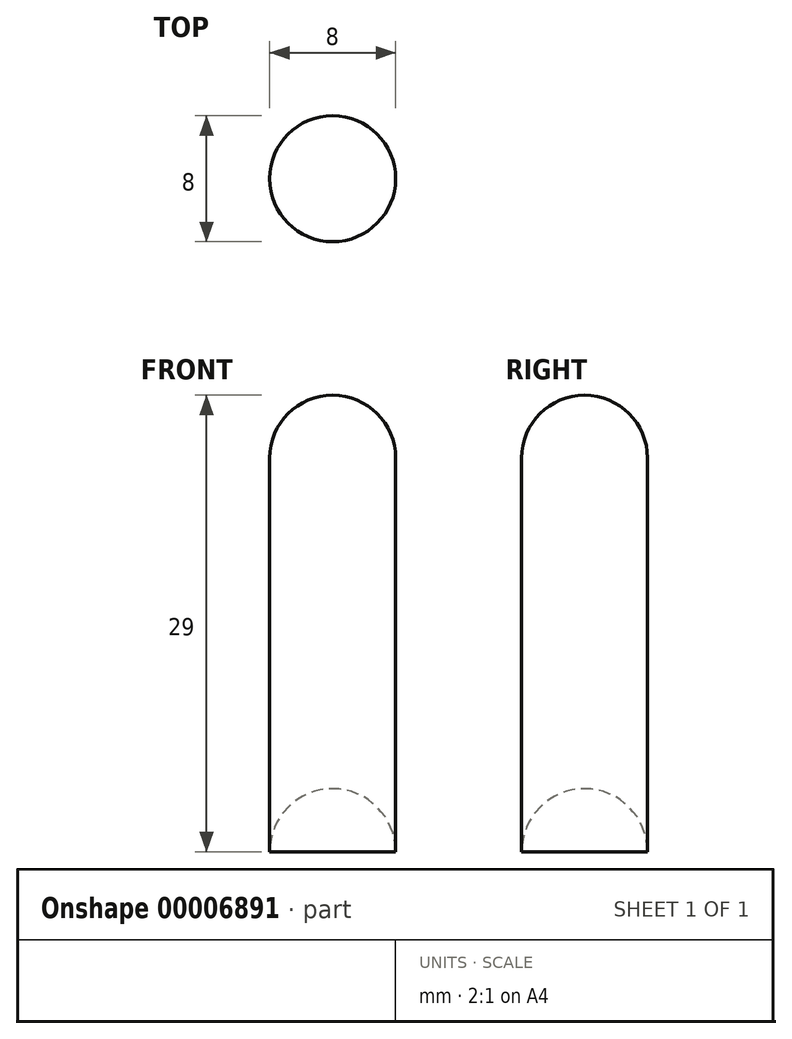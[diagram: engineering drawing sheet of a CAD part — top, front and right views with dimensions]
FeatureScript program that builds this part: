
annotation { "Feature Type Name" : "Feature", "Feature Type Description" : "" }
export const myFeature = defineFeature(function(context is Context, id is Id, definition is map)
    precondition{}
    {
        {
            var Q0;
            Q0=qCreatedBy(makeId("Top.planeOp"),FACE);
            var sketch = newSketch(context, id + "F0", { "sketchPlane" : qUnion([Q0])});
            skCircle(sketch, "E0", {"center": v(0, 0) * mm, "radius": 4 * mm});
            skSolve(sketch);
        }
        {
            var Q0;
            Q0 = qSketchRegion(id + "F0", true);
            extrude(context, id + "F1", {"entities" : qUnion([Q0]), "depth" : 25 * mm});
        }
        {
            var Q0;
            Q0=makeQuery(id+"F1.opExtrude","CAP_FACE",FACE,{"disambiguationData":[OSD([sQuery(id+"F0.wireOp",EDGE,"E0")])],"isStart":false});
            var sketch = newSketch(context, id + "F2", { "sketchPlane" : qUnion([Q0])});
            skCircle(sketch, "E1", {"center": v(0, 0) * mm, "radius": 4 * mm});
            skLineSegment(sketch, "E2", {"start": v(0, 4) * mm, "end": v(0, -4) * mm});
            skSolve(sketch);
        }
        {
            var Q0;
            {var subQ0=sQuery(id+"F2.wireOp",EDGE,"E2");Q0=makeQuery(id+"F2.imprint","IMPRINT",FACE,{"disambiguationData":[TD([[makeQuery(id+"F2.imprint","IMPRINT",EDGE,{"derivedFrom":subQ0}),-1.0]])]});}
            var Q1;
            Q1=sQuery(id+"F2.wireOp",EDGE,"E2");
            revolve(context, id + "F3", {"operationType" : NewBodyOperationType.ADD, "entities" : qUnion([Q0]), "axis" : qUnion([Q1]), "revolveType" : RevolveType.FULL});
        }
        {
            var Q0;
            Q0=makeQuery(id+"F1.opExtrude","CAP_FACE",FACE,{"disambiguationData":[OSD([sQuery(id+"F0.wireOp",EDGE,"E0")])],"isStart":true});
            var sketch = newSketch(context, id + "F4", { "sketchPlane" : qUnion([Q0])});
            skLineSegment(sketch, "E3", {"start": v(4, 0) * mm, "end": v(-4, 0) * mm});
            skSolve(sketch);
        }
        {
            var Q0;
            Q0 = qSketchRegion(id + "F4", true);
            var Q1;
            {var subQ1=sQuery(id+"F4.wireOp",EDGE,"E3");Q1=makeQuery(id+"F4.imprint","IMPRINT",FACE,{"disambiguationData":[TD([[makeQuery(id+"F4.imprint","IMPRINT",EDGE,{"derivedFrom":subQ1}),1.0]])]});}
            var Q2;
            Q2=sQuery(id+"F4.wireOp",EDGE,"E3");
            revolve(context, id + "F5", {"operationType" : NewBodyOperationType.REMOVE, "entities" : qUnion([Q0, Q1]), "axis" : qUnion([Q2]), "revolveType" : RevolveType.FULL, "oppositeDirection" : true});
        }
    });
